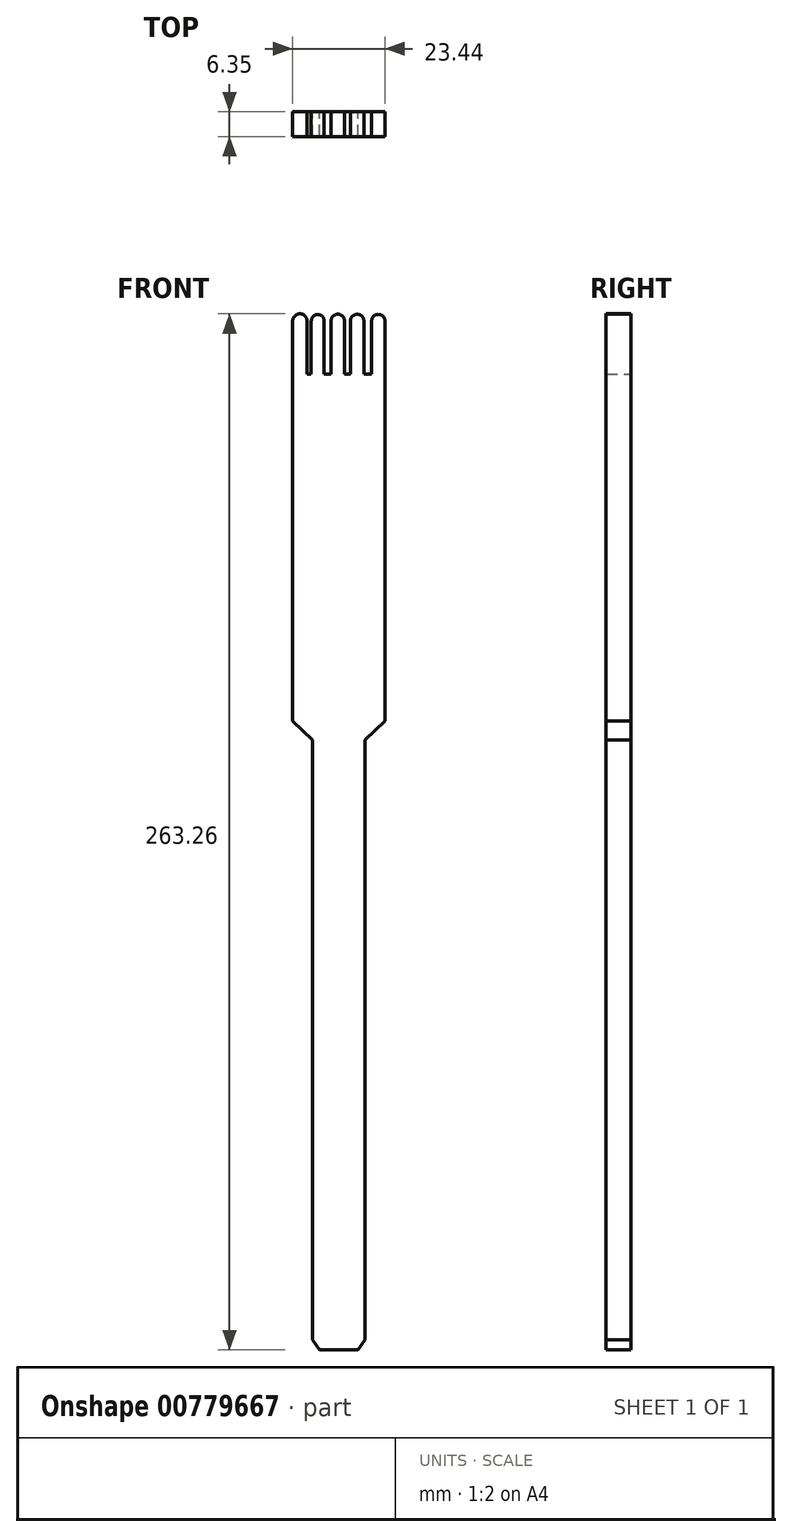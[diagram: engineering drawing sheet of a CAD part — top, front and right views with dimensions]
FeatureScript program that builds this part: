
annotation { "Feature Type Name" : "Feature", "Feature Type Description" : "" }
export const myFeature = defineFeature(function(context is Context, id is Id, definition is map)
    precondition{}
    {
        {
            var Q0;
            Q0=qCreatedBy(makeId("Front.planeOp"),FACE);
            var sketch = newSketch(context, id + "F0", { "sketchPlane" : qUnion([Q0])});
            skLineSegment(sketch, "E0", {"start": v(-8.09, -139.33) * mm, "end": v(-6.37, -141.9) * mm});
            skLineSegment(sketch, "E1", {"start": v(5.17, -139.33) * mm, "end": v(3.48, -141.9) * mm});
            skLineSegment(sketch, "E2", {"start": v(3.48, -141.9) * mm, "end": v(-6.37, -141.9) * mm});
            skLineSegment(sketch, "E3", {"start": v(-8.09, -139.33) * mm, "end": v(-8.09, 13.07) * mm});
            skLineSegment(sketch, "E4", {"start": v(5.17, -139.33) * mm, "end": v(5.17, 13.07) * mm});
            skLineSegment(sketch, "E5", {"start": v(5.17, 13.07) * mm, "end": v(10.26, 17.93) * mm});
            skLineSegment(sketch, "E6", {"start": v(-8.09, 13.07) * mm, "end": v(-13.18, 17.93) * mm});
            skLineSegment(sketch, "E7", {"start": v(-13.18, 17.93) * mm, "end": v(-13.18, 119.53) * mm});
            skLineSegment(sketch, "E8", {"start": v(10.26, 17.93) * mm, "end": v(10.26, 119.53) * mm});
            skLineSegment(sketch, "E9", {"start": v(6.9, 119.53) * mm, "end": v(6.9, 106.05) * mm});
            skLineSegment(sketch, "E10", {"start": v(6.9, 106.05) * mm, "end": v(4.9, 106.05) * mm});
            skLineSegment(sketch, "E11", {"start": v(4.9, 106.05) * mm, "end": v(4.9, 119.53) * mm});
            skLineSegment(sketch, "E12", {"start": v(1.5, 119.53) * mm, "end": v(1.5, 106.05) * mm});
            skLineSegment(sketch, "E13", {"start": v(1.5, 106.05) * mm, "end": v(0, 106.05) * mm});
            skLineSegment(sketch, "E14", {"start": v(0, 106.05) * mm, "end": v(0, 119.53) * mm});
            skLineSegment(sketch, "E15", {"start": v(-3.42, 119.53) * mm, "end": v(-3.42, 106.05) * mm});
            skLineSegment(sketch, "E16", {"start": v(-3.42, 106.05) * mm, "end": v(-5.18, 106.05) * mm});
            skLineSegment(sketch, "E17", {"start": v(-5.18, 106.05) * mm, "end": v(-5.18, 119.53) * mm});
            skLineSegment(sketch, "E18", {"start": v(-8.46, 119.53) * mm, "end": v(-8.46, 106.05) * mm});
            skLineSegment(sketch, "E19", {"start": v(-8.46, 106.05) * mm, "end": v(-9.51, 106.05) * mm});
            skLineSegment(sketch, "E20", {"start": v(-9.51, 106.05) * mm, "end": v(-9.51, 119.53) * mm});
            skArc(sketch, "E21", {"start": v(-9.51, 119.53) * mm, "mid": v(-11.34, 121.36) * mm, "end": v(-13.18, 119.53) * mm});
            skArc(sketch, "E22", {"start": v(-5.18, 119.53) * mm, "mid": v(-6.82, 121.17) * mm, "end": v(-8.46, 119.53) * mm});
            skArc(sketch, "E23", {"start": v(0, 119.53) * mm, "mid": v(-1.7, 121.24) * mm, "end": v(-3.42, 119.53) * mm});
            skArc(sketch, "E24", {"start": v(4.9, 119.53) * mm, "mid": v(3.2, 121.23) * mm, "end": v(1.5, 119.53) * mm});
            skArc(sketch, "E25", {"start": v(10.26, 119.53) * mm, "mid": v(8.58, 121.21) * mm, "end": v(6.9, 119.53) * mm});
            skSolve(sketch);
        }
        {
            var Q0;
            Q0 = qSketchRegion(id + "F0", true);
            extrude(context, id + "F1", {"entities" : qUnion([Q0]), "depth" : 6.35 * mm, "offsetDistance" : 25.4 * mm});
        }
    });
